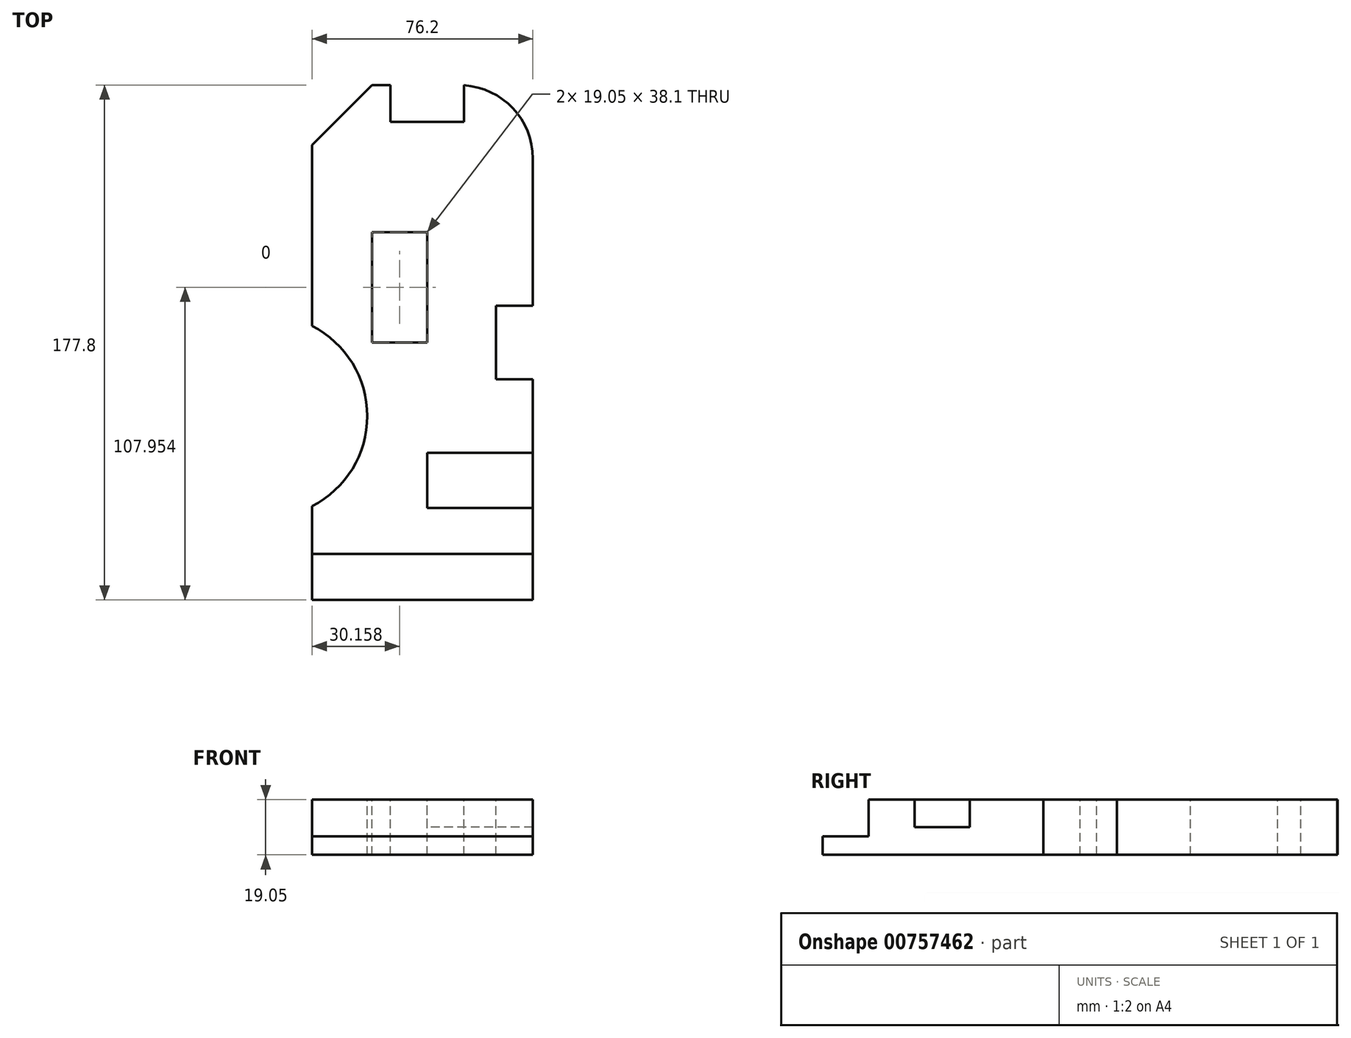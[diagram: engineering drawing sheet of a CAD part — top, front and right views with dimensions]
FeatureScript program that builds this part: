
annotation { "Feature Type Name" : "Feature", "Feature Type Description" : "" }
export const myFeature = defineFeature(function(context is Context, id is Id, definition is map)
    precondition{}
    {
        {
            var Q0;
            Q0=qCreatedBy(makeId("Top.planeOp"),FACE);
            var sketch = newSketch(context, id + "F0", { "sketchPlane" : qUnion([Q0])});
            skLineSegment(sketch, "E0", {"start": v(-82, -72.72) * mm, "end": v(-5.8, -72.72) * mm});
            skLineSegment(sketch, "E1", {"start": v(-5.8, -72.72) * mm, "end": v(-5.8, 105.08) * mm});
            skLineSegment(sketch, "E2", {"start": v(-5.8, 105.08) * mm, "end": v(-82, 105.08) * mm});
            skLineSegment(sketch, "E3", {"start": v(-82, 105.08) * mm, "end": v(-82, -72.72) * mm});
            skSolve(sketch);
        }
        {
            var Q0;
            Q0=makeQuery(id+"F0.imprint","IMPRINT",FACE,{"disambiguationData":[TD([[makeQuery(id+"F0.imprint","IMPRINT",EDGE,{"derivedFrom":sQuery(id+"F0.wireOp",EDGE,"E0")}),1.0]])]});
            extrude(context, id + "F1", {"entities" : qUnion([Q0]), "depth" : 19.05 * mm, "offsetDistance" : 25.4 * mm});
        }
        {
            var Q0;
            Q0=makeQuery(id+"F1.opExtrude","SWEPT_EDGE",EDGE,{"disambiguationData":[OSD([sQuery(id+"F0.wireOp",EDGE,"E1"),sQuery(id+"F0.wireOp",EDGE,"E2")])]});
            fillet(context, id + "F2", {"entities" : qUnion([Q0]), "radius" : 25.4 * mm, "tangentPropagation" : true, "allowEdgeOverflow" : false});
        }
        {
            var Q0;
            Q0=makeQuery(id+"F1.opExtrude","CAP_FACE",FACE,{"disambiguationData":[OSD([sQuery(id+"F0.wireOp",EDGE,"E0"),sQuery(id+"F0.wireOp",EDGE,"E1"),sQuery(id+"F0.wireOp",EDGE,"E2"),sQuery(id+"F0.wireOp",EDGE,"E3")])],"isStart":false});
            var sketch = newSketch(context, id + "F3", { "sketchPlane" : qUnion([Q0])});
            skLineSegment(sketch, "E4", {"start": v(-82, 105.08) * mm, "end": v(-82, 84.45) * mm});
            skLineSegment(sketch, "E5", {"start": v(-82, 84.45) * mm, "end": v(-61.37, 105.08) * mm});
            skLineSegment(sketch, "E6", {"start": v(-82, 105.08) * mm, "end": v(-61.37, 105.08) * mm});
            skSolve(sketch);
        }
        {
            var Q0;
            Q0 = qSketchRegion(id + "F3", true);
            extrude(context, id + "F4", {"entities" : qUnion([Q0]), "operationType" : NewBodyOperationType.REMOVE, "oppositeDirection" : true, "depth" : 25.4 * mm, "offsetDistance" : 25.4 * mm});
        }
        {
            var Q0;
            Q0=makeQuery(id+"F1.opExtrude","CAP_FACE",FACE,{"disambiguationData":[OSD([sQuery(id+"F0.wireOp",EDGE,"E0"),sQuery(id+"F0.wireOp",EDGE,"E1"),sQuery(id+"F0.wireOp",EDGE,"E2"),sQuery(id+"F0.wireOp",EDGE,"E3")])],"isStart":false});
            var sketch = newSketch(context, id + "F5", { "sketchPlane" : qUnion([Q0])});
            skLineSegment(sketch, "E7", {"start": v(-55.02, 105.08) * mm, "end": v(-55.02, 92.38) * mm});
            skLineSegment(sketch, "E8", {"start": v(-55.02, 92.38) * mm, "end": v(-29.62, 92.38) * mm});
            skLineSegment(sketch, "E9", {"start": v(-29.62, 92.38) * mm, "end": v(-29.62, 105.08) * mm});
            skSolve(sketch);
        }
        {
            var Q0;
            Q0 = qSketchRegion(id + "F5", true);
            var Q1;
            {var subQ8=sQuery(id+"F5.wireOp",EDGE,"E7");Q1=makeQuery(id+"F5.imprint","IMPRINT",FACE,{"disambiguationData":[TD([[makeQuery(id+"F5.imprint","IMPRINT",EDGE,{"derivedFrom":subQ8}),1.0]])]});}
            extrude(context, id + "F6", {"entities" : qUnion([Q0, Q1]), "operationType" : NewBodyOperationType.REMOVE, "oppositeDirection" : true, "depth" : 25.4 * mm, "offsetDistance" : 25.4 * mm});
        }
        {
            var Q0;
            Q0=makeQuery(id+"F1.opExtrude","CAP_FACE",FACE,{"disambiguationData":[OSD([sQuery(id+"F0.wireOp",EDGE,"E0"),sQuery(id+"F0.wireOp",EDGE,"E1"),sQuery(id+"F0.wireOp",EDGE,"E2"),sQuery(id+"F0.wireOp",EDGE,"E3")])],"isStart":false});
            var sketch = newSketch(context, id + "F7", { "sketchPlane" : qUnion([Q0])});
            skLineSegment(sketch, "E10", {"start": v(-82, -72.72) * mm, "end": v(-5.8, -72.72) * mm});
            skLineSegment(sketch, "E11", {"start": v(-5.8, -72.72) * mm, "end": v(-5.8, -56.84) * mm});
            skLineSegment(sketch, "E12", {"start": v(-5.8, -56.84) * mm, "end": v(-82, -56.84) * mm});
            skLineSegment(sketch, "E13", {"start": v(-82, -56.84) * mm, "end": v(-82, -72.72) * mm});
            skSolve(sketch);
        }
        {
            var Q0;
            Q0=makeQuery(id+"F7.imprint","IMPRINT",FACE,{"disambiguationData":[TD([[makeQuery(id+"F7.imprint","IMPRINT",EDGE,{"derivedFrom":sQuery(id+"F7.wireOp",EDGE,"E10")}),1.0]])]});
            extrude(context, id + "F8", {"entities" : qUnion([Q0]), "operationType" : NewBodyOperationType.REMOVE, "oppositeDirection" : true, "depth" : 12.7 * mm, "offsetDistance" : 25.4 * mm});
        }
        {
            var Q0;
            Q0=makeQuery(id+"F1.opExtrude","CAP_FACE",FACE,{"disambiguationData":[OSD([sQuery(id+"F0.wireOp",EDGE,"E0"),sQuery(id+"F0.wireOp",EDGE,"E1"),sQuery(id+"F0.wireOp",EDGE,"E2"),sQuery(id+"F0.wireOp",EDGE,"E3")])],"isStart":false});
            var sketch = newSketch(context, id + "F9", { "sketchPlane" : qUnion([Q0])});
            skLineSegment(sketch, "E14", {"start": v(-5.8, -40.97) * mm, "end": v(-42.32, -40.97) * mm});
            skLineSegment(sketch, "E15", {"start": v(-42.32, -40.97) * mm, "end": v(-42.32, -21.92) * mm});
            skLineSegment(sketch, "E16", {"start": v(-42.32, -21.92) * mm, "end": v(-5.8, -21.92) * mm});
            skSolve(sketch);
        }
        {
            var Q0;
            Q0 = qSketchRegion(id + "F9", true);
            var Q1;
            {var subQ0=sQuery(id+"F9.wireOp",EDGE,"E14");Q1=makeQuery(id+"F9.imprint","IMPRINT",FACE,{"disambiguationData":[TD([[makeQuery(id+"F9.imprint","IMPRINT",EDGE,{"derivedFrom":subQ0}),-1.0]])]});}
            extrude(context, id + "F10", {"entities" : qUnion([Q0, Q1]), "operationType" : NewBodyOperationType.REMOVE, "oppositeDirection" : true, "depth" : 9.52 * mm, "offsetDistance" : 25.4 * mm});
        }
        {
            var Q0;
            Q0=makeQuery(id+"F1.opExtrude","CAP_FACE",FACE,{"disambiguationData":[OSD([sQuery(id+"F0.wireOp",EDGE,"E0"),sQuery(id+"F0.wireOp",EDGE,"E1"),sQuery(id+"F0.wireOp",EDGE,"E2"),sQuery(id+"F0.wireOp",EDGE,"E3")])],"isStart":false});
            var sketch = newSketch(context, id + "F11", { "sketchPlane" : qUnion([Q0])});
            skLineSegment(sketch, "E17", {"start": v(-5.8, 3.48) * mm, "end": v(-18.5, 3.48) * mm});
            skLineSegment(sketch, "E18", {"start": v(-18.5, 3.48) * mm, "end": v(-18.5, 28.88) * mm});
            skLineSegment(sketch, "E19", {"start": v(-18.5, 28.88) * mm, "end": v(-5.8, 28.88) * mm});
            skSolve(sketch);
        }
        {
            var Q0;
            Q0 = qSketchRegion(id + "F11", true);
            var Q1;
            {var subQ0=sQuery(id+"F11.wireOp",EDGE,"E17");Q1=makeQuery(id+"F11.imprint","IMPRINT",FACE,{"disambiguationData":[TD([[makeQuery(id+"F11.imprint","IMPRINT",EDGE,{"derivedFrom":subQ0}),-1.0]])]});}
            extrude(context, id + "F12", {"entities" : qUnion([Q0, Q1]), "operationType" : NewBodyOperationType.REMOVE, "oppositeDirection" : true, "depth" : 25.4 * mm, "offsetDistance" : 25.4 * mm});
        }
        {
            var Q0;
            Q0=makeQuery(id+"F1.opExtrude","CAP_FACE",FACE,{"disambiguationData":[OSD([sQuery(id+"F0.wireOp",EDGE,"E0"),sQuery(id+"F0.wireOp",EDGE,"E1"),sQuery(id+"F0.wireOp",EDGE,"E2"),sQuery(id+"F0.wireOp",EDGE,"E3")])],"isStart":false});
            var sketch = newSketch(context, id + "F13", { "sketchPlane" : qUnion([Q0])});
            skLineSegment(sketch, "E20", {"start": v(-82, -56.84) * mm, "end": v(-82, -40.97) * mm});
            skLineSegment(sketch, "E21", {"start": v(-62.95, -9.22) * mm, "end": v(-97.88, -9.22) * mm});
            skCircle(sketch, "E22", {"center": v(-97.88, -9.22) * mm, "radius": 34.92 * mm});
            skSolve(sketch);
        }
        {
            var Q0;
            Q0 = qSketchRegion(id + "F13", true);
            extrude(context, id + "F14", {"entities" : qUnion([Q0]), "operationType" : NewBodyOperationType.REMOVE, "oppositeDirection" : true, "depth" : 25.4 * mm, "offsetDistance" : 25.4 * mm});
        }
        {
            var Q0;
            Q0=makeQuery(id+"F1.opExtrude","CAP_FACE",FACE,{"disambiguationData":[OSD([sQuery(id+"F0.wireOp",EDGE,"E0"),sQuery(id+"F0.wireOp",EDGE,"E1"),sQuery(id+"F0.wireOp",EDGE,"E2"),sQuery(id+"F0.wireOp",EDGE,"E3")])],"isStart":false});
            var sketch = newSketch(context, id + "F15", { "sketchPlane" : qUnion([Q0])});
            skLineSegment(sketch, "E23", {"start": v(-42.32, 16.18) * mm, "end": v(-42.32, 54.28) * mm});
            skLineSegment(sketch, "E24", {"start": v(-42.32, 54.28) * mm, "end": v(-61.37, 54.28) * mm});
            skLineSegment(sketch, "E25", {"start": v(-61.37, 54.28) * mm, "end": v(-61.37, 16.18) * mm});
            skLineSegment(sketch, "E26", {"start": v(-61.37, 16.18) * mm, "end": v(-42.32, 16.18) * mm});
            skSolve(sketch);
        }
        {
            var Q0;
            Q0 = qSketchRegion(id + "F15", true);
            extrude(context, id + "F16", {"entities" : qUnion([Q0]), "operationType" : NewBodyOperationType.REMOVE, "oppositeDirection" : true, "depth" : 25.4 * mm, "offsetDistance" : 25.4 * mm});
        }
    });
